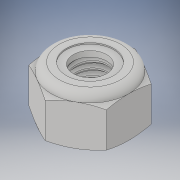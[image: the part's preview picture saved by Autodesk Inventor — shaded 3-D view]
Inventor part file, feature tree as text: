
AUTODESK INVENTOR PART (.ipt)
format: ipt  version: 2018 (Build 220112000, 112)  size: 308,736 bytes
history: native  units: in
note: dims shown in document units (in); Inventor stores cm internally (conversion verified against a paired STEP export)
features: other x1, revolve x1
ambient origin geometry x8: Origin, YZ Plane, XZ Plane, XY Plane, X Axis, Y Axis, Z Axis, Center Point
bodies: Solid1 (feature_tree), Solid2 (feature_tree)
feature tree (2):
  other  "Cut-Revolve4"
  revolve  "Revolve2"  [1 undecoded]
note: 1 required parameter value undecoded (feature->parameter linkage not recoverable at this tier; creation-order binding heuristic only, values carry confidence <= 0.55)
